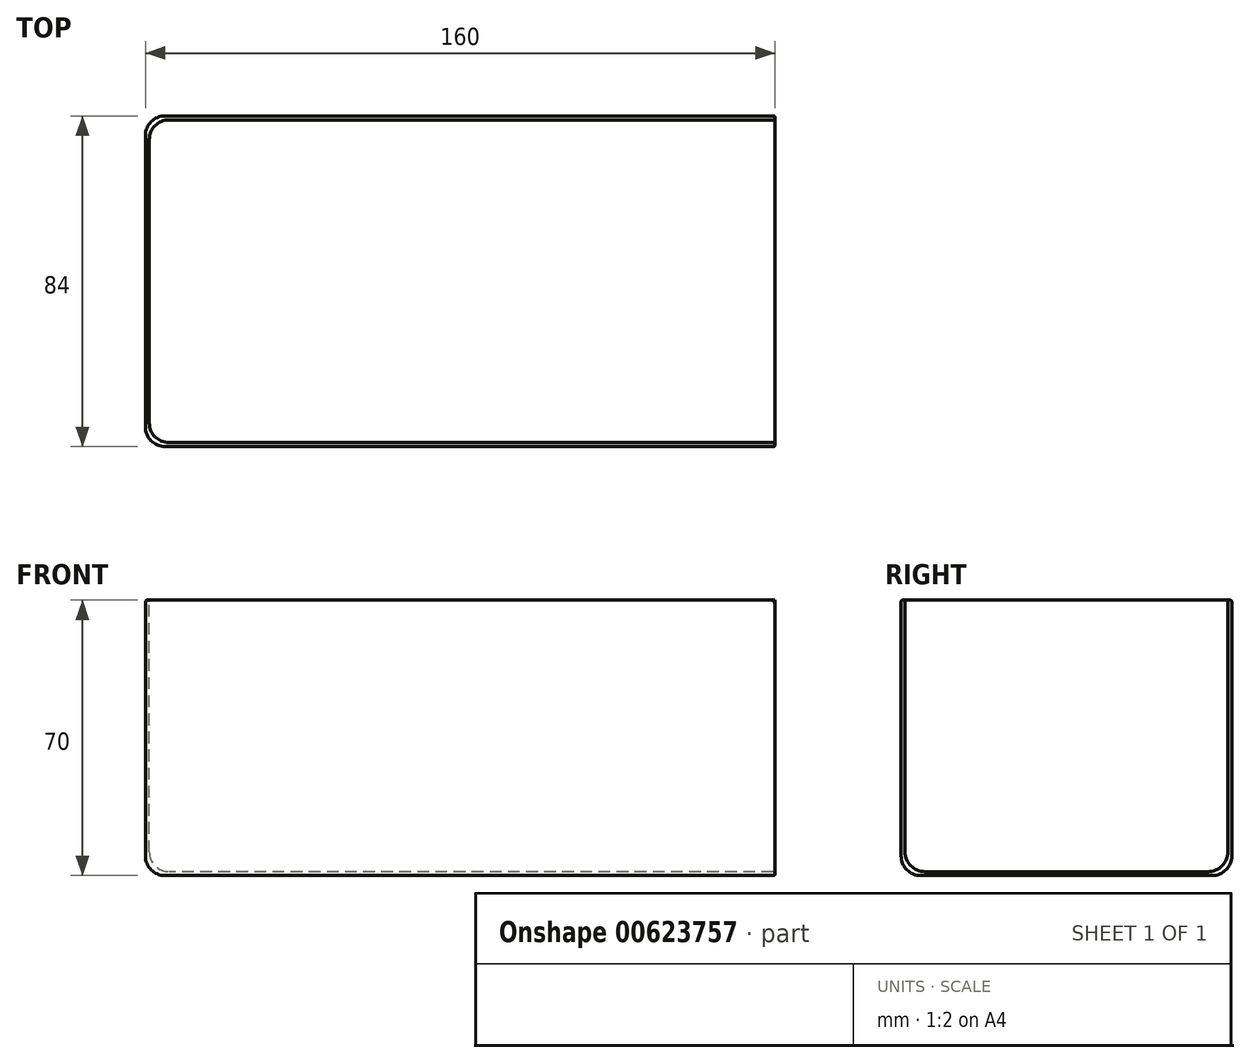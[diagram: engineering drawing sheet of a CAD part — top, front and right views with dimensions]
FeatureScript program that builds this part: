
annotation { "Feature Type Name" : "Feature", "Feature Type Description" : "" }
export const myFeature = defineFeature(function(context is Context, id is Id, definition is map)
    precondition{}
    {
        {
            var Q0;
            Q0=qCreatedBy(makeId("Top.planeOp"),FACE);
            var sketch = newSketch(context, id + "F0", { "sketchPlane" : qUnion([Q0])});
            skLineSegment(sketch, "E0.bottom", {"start": v(80, -42) * mm, "end": v(-80, -42) * mm});
            skLineSegment(sketch, "E0.top", {"start": v(80, 42) * mm, "end": v(-80, 42) * mm});
            skLineSegment(sketch, "E0.left", {"start": v(80, -42) * mm, "end": v(80, 42) * mm});
            skLineSegment(sketch, "E0.right", {"start": v(-80, -42) * mm, "end": v(-80, 42) * mm});
            skPoint(sketch, "E0.middle", {"position": v(0, 0) * mm});
            skSolve(sketch);
        }
        {
            var Q0;
            Q0=makeQuery(id+"F0.imprint","IMPRINT",FACE,{"disambiguationData":[TD([[makeQuery(id+"F0.imprint","IMPRINT",EDGE,{"derivedFrom":sQuery(id+"F0.wireOp",EDGE,"E0.bottom")}),-1.0]])]});
            extrude(context, id + "F1", {"entities" : qUnion([Q0]), "depth" : 70 * mm, "offsetDistance" : 25 * mm});
        }
        {
            var Q0;
            Q0=makeQuery(id+"F1.opExtrude","CAP_FACE",FACE,{"disambiguationData":[OSD([sQuery(id+"F0.wireOp",EDGE,"E0.bottom"),sQuery(id+"F0.wireOp",EDGE,"E0.top"),sQuery(id+"F0.wireOp",EDGE,"E0.left"),sQuery(id+"F0.wireOp",EDGE,"E0.right")])],"isStart":false});
            var sketch = newSketch(context, id + "F2", { "sketchPlane" : qUnion([Q0])});
            skLineSegment(sketch, "E1.bottom", {"start": v(80, 41) * mm, "end": v(-79, 41) * mm});
            skLineSegment(sketch, "E1.top", {"start": v(80, -41) * mm, "end": v(-79, -41) * mm});
            skLineSegment(sketch, "E1.left", {"start": v(80, 41) * mm, "end": v(80, -41) * mm});
            skLineSegment(sketch, "E1.right", {"start": v(-79, 41) * mm, "end": v(-79, -41) * mm});
            skLineSegment(sketch, "E2", {"start": v(30.94, -41) * mm, "end": v(30.94, -42) * mm});
            skSolve(sketch);
        }
        {
            var Q0;
            Q0=makeQuery(id+"F2.imprint","IMPRINT",FACE,{"disambiguationData":[TD([[makeQuery(id+"F2.imprint","IMPRINT",EDGE,{"derivedFrom":sQuery(id+"F2.wireOp",EDGE,"E1.bottom")}),1.0]])]});
            extrude(context, id + "F3", {"entities" : qUnion([Q0]), "operationType" : NewBodyOperationType.REMOVE, "oppositeDirection" : true, "depth" : 69 * mm, "offsetDistance" : 25 * mm});
        }
        {
            var Q0;
            Q0=makeQuery(id+"F3.boolean.opBoolean","COPY",EDGE,{"derivedFrom":makeQuery(id+"F3.opExtrude","CAP_EDGE",EDGE,{"disambiguationData":[OSD([sQuery(id+"F2.wireOp",EDGE,"E1.right")])],"isStart":false})});
            var Q1;
            Q1=makeQuery(id+"F3.boolean.opBoolean","COPY",EDGE,{"derivedFrom":makeQuery(id+"F3.opExtrude","CAP_EDGE",EDGE,{"disambiguationData":[OSD([sQuery(id+"F2.wireOp",EDGE,"E1.top")])],"isStart":false})});
            var Q2;
            Q2=makeQuery(id+"F3.boolean.opBoolean","COPY",EDGE,{"derivedFrom":makeQuery(id+"F3.opExtrude","CAP_EDGE",EDGE,{"disambiguationData":[OSD([sQuery(id+"F2.wireOp",EDGE,"E1.bottom")])],"isStart":false})});
            fillet(context, id + "F4", {"entities" : qUnion([Q0, Q1, Q2]), "radius" : 5 * mm, "tangentPropagation" : true, "allowEdgeOverflow" : false});
        }
        {
            var Q0;
            Q0=makeQuery(id+"F1.opExtrude","CAP_EDGE",EDGE,{"disambiguationData":[OSD([sQuery(id+"F0.wireOp",EDGE,"E0.right")])],"isStart":true});
            var Q1;
            Q1=makeQuery(id+"F1.opExtrude","CAP_EDGE",EDGE,{"disambiguationData":[OSD([sQuery(id+"F0.wireOp",EDGE,"E0.top")])],"isStart":true});
            var Q2;
            Q2=makeQuery(id+"F1.opExtrude","CAP_EDGE",EDGE,{"disambiguationData":[OSD([sQuery(id+"F0.wireOp",EDGE,"E0.bottom")])],"isStart":true});
            fillet(context, id + "F5", {"entities" : qUnion([Q0, Q1, Q2]), "radius" : 5 * mm, "tangentPropagation" : true, "allowEdgeOverflow" : false});
        }
        {
            var Q0;
            Q0=makeQuery(id+"F3.boolean.opBoolean","COPY",EDGE,{"derivedFrom":makeQuery(id+"F3.opExtrude","SWEPT_EDGE",EDGE,{"disambiguationData":[OSD([sQuery(id+"F2.wireOp",EDGE,"E1.bottom"),sQuery(id+"F2.wireOp",EDGE,"E1.right")])]})});
            var Q1;
            Q1=makeQuery(id+"F3.boolean.opBoolean","COPY",EDGE,{"derivedFrom":makeQuery(id+"F3.opExtrude","SWEPT_EDGE",EDGE,{"disambiguationData":[OSD([sQuery(id+"F2.wireOp",EDGE,"E1.top"),sQuery(id+"F2.wireOp",EDGE,"E1.right")])]})});
            fillet(context, id + "F6", {"entities" : qUnion([Q0, Q1]), "radius" : 5 * mm, "tangentPropagation" : true, "allowEdgeOverflow" : false});
        }
        {
            var Q0;
            Q0=makeQuery(id+"F1.opExtrude","SWEPT_EDGE",EDGE,{"disambiguationData":[OSD([sQuery(id+"F0.wireOp",EDGE,"E0.top"),sQuery(id+"F0.wireOp",EDGE,"E0.right")])]});
            var Q1;
            Q1=makeQuery(id+"F1.opExtrude","SWEPT_EDGE",EDGE,{"disambiguationData":[OSD([sQuery(id+"F0.wireOp",EDGE,"E0.bottom"),sQuery(id+"F0.wireOp",EDGE,"E0.right")])]});
            fillet(context, id + "F7", {"entities" : qUnion([Q0, Q1]), "radius" : 5 * mm, "tangentPropagation" : true, "allowEdgeOverflow" : false});
        }
        {
            var Q0;
            Q0=makeQuery(id+"F3.boolean.opBoolean","COPY",EDGE,{"derivedFrom":makeQuery(id+"F3.opExtrude","CAP_EDGE",EDGE,{"disambiguationData":[OSD([sQuery(id+"F2.wireOp",EDGE,"E1.top")])],"isStart":true})});
            var Q1;
            Q1=makeQuery(id+"F3.boolean.opBoolean","COPY",EDGE,{"derivedFrom":makeQuery(id+"F3.opExtrude","CAP_EDGE",EDGE,{"disambiguationData":[OSD([sQuery(id+"F2.wireOp",EDGE,"E1.right")])],"isStart":true})});
            var Q2;
            Q2=makeQuery(id+"F3.boolean.opBoolean","COPY",EDGE,{"derivedFrom":makeQuery(id+"F3.opExtrude","CAP_EDGE",EDGE,{"disambiguationData":[OSD([sQuery(id+"F2.wireOp",EDGE,"E1.bottom")])],"isStart":true})});
            var Q3;
            Q3=makeQuery(id+"F6.opFillet","BLEND_EDGE",EDGE,{"blendedFrom":[makeQuery(id+"F3.boolean.opBoolean","COPY",EDGE,{"derivedFrom":makeQuery(id+"F3.opExtrude","SWEPT_EDGE",EDGE,{"disambiguationData":[OSD([sQuery(id+"F2.wireOp",EDGE,"E1.bottom"),sQuery(id+"F2.wireOp",EDGE,"E1.right")])]})}),makeQuery(id+"F1.opExtrude","CAP_FACE",FACE,{"disambiguationData":[OSD([sQuery(id+"F0.wireOp",EDGE,"E0.bottom"),sQuery(id+"F0.wireOp",EDGE,"E0.top"),sQuery(id+"F0.wireOp",EDGE,"E0.left"),sQuery(id+"F0.wireOp",EDGE,"E0.right")])],"isStart":false})],"blendedInto":[makeQuery(id+"F1.opExtrude","CAP_FACE",FACE,{"disambiguationData":[OSD([sQuery(id+"F0.wireOp",EDGE,"E0.bottom"),sQuery(id+"F0.wireOp",EDGE,"E0.top"),sQuery(id+"F0.wireOp",EDGE,"E0.left"),sQuery(id+"F0.wireOp",EDGE,"E0.right")])],"isStart":false})]});
            var Q4;
            {var subQ0=sQuery(id+"F0.wireOp",EDGE,"E0.right");var subQ1=sQuery(id+"F0.wireOp",EDGE,"E0.bottom");Q4=makeQuery(id+"F7.opFillet","BLEND_EDGE",EDGE,{"blendedFrom":[makeQuery(id+"F1.opExtrude","SWEPT_EDGE",EDGE,{"disambiguationData":[OSD([subQ1,subQ0])]}),makeQuery(id+"F1.opExtrude","CAP_FACE",FACE,{"disambiguationData":[OSD([subQ1,sQuery(id+"F0.wireOp",EDGE,"E0.top"),sQuery(id+"F0.wireOp",EDGE,"E0.left"),subQ0])],"isStart":false})],"blendedInto":[makeQuery(id+"F1.opExtrude","CAP_FACE",FACE,{"disambiguationData":[OSD([subQ1,sQuery(id+"F0.wireOp",EDGE,"E0.top"),sQuery(id+"F0.wireOp",EDGE,"E0.left"),subQ0])],"isStart":false})]});}
            var Q5;
            Q5=makeQuery(id+"F1.opExtrude","SWEPT_EDGE",EDGE,{"disambiguationData":[OSD([sQuery(id+"F0.wireOp",EDGE,"E0.top"),sQuery(id+"F0.wireOp",EDGE,"E0.left")])]});
            var Q6;
            Q6=makeQuery(id+"F1.opExtrude","SWEPT_EDGE",EDGE,{"disambiguationData":[OSD([sQuery(id+"F0.wireOp",EDGE,"E0.bottom"),sQuery(id+"F0.wireOp",EDGE,"E0.left")])]});
            var Q7;
            Q7=makeQuery(id+"F4.opFillet","BLEND_EDGE",EDGE,{"blendedFrom":[makeQuery(id+"F3.boolean.opBoolean","COPY",EDGE,{"derivedFrom":makeQuery(id+"F3.opExtrude","CAP_EDGE",EDGE,{"disambiguationData":[OSD([sQuery(id+"F2.wireOp",EDGE,"E1.top")])],"isStart":false})}),makeQuery(id+"F1.opExtrude","SWEPT_FACE",FACE,{"disambiguationData":[OSD([sQuery(id+"F0.wireOp",EDGE,"E0.left")])]})],"blendedInto":[makeQuery(id+"F1.opExtrude","SWEPT_FACE",FACE,{"disambiguationData":[OSD([sQuery(id+"F0.wireOp",EDGE,"E0.left")])]})]});
            var Q8;
            Q8=makeQuery(id+"F4.opFillet","BLEND_EDGE",EDGE,{"blendedFrom":[makeQuery(id+"F3.boolean.opBoolean","COPY",EDGE,{"derivedFrom":makeQuery(id+"F3.opExtrude","CAP_EDGE",EDGE,{"disambiguationData":[OSD([sQuery(id+"F2.wireOp",EDGE,"E1.bottom")])],"isStart":false})}),makeQuery(id+"F1.opExtrude","SWEPT_FACE",FACE,{"disambiguationData":[OSD([sQuery(id+"F0.wireOp",EDGE,"E0.left")])]})],"blendedInto":[makeQuery(id+"F1.opExtrude","SWEPT_FACE",FACE,{"disambiguationData":[OSD([sQuery(id+"F0.wireOp",EDGE,"E0.left")])]})]});
            var Q9;
            Q9=makeQuery(id+"F1.opExtrude","CAP_EDGE",EDGE,{"disambiguationData":[OSD([sQuery(id+"F0.wireOp",EDGE,"E0.left")])],"isStart":true});
            fillet(context, id + "F8", {"entities" : qUnion([Q0, Q1, Q2, Q3, Q4, Q5, Q6, Q7, Q8, Q9]), "radius" : .5 * mm, "tangentPropagation" : true, "allowEdgeOverflow" : false});
        }
    });
